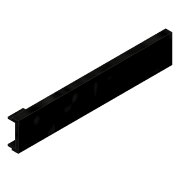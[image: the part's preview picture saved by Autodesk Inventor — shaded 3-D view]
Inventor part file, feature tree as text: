
AUTODESK INVENTOR PART (.ipt)
format: ipt  version: 2017 (Build 210142000, 142)  size: 198,144 bytes
history: native  units: in
note: dims shown in document units (in); Inventor stores cm internally (conversion verified against a paired STEP export)
features: sketch x6, extrude x6, projected_geometry x6, other x3, plane x2, reference x1
ambient origin geometry x8: Origin, YZ Plane, XZ Plane, XY Plane, X Axis, Y Axis, Z Axis, Center Point
bodies: Solid1 (feature_tree)
feature tree (24):
  sketch  "Sketch1"  dims[d0=0.02in d1=0.02in]
  plane  "Work Plane1"
  extrude  "Extrusion1"  Depth=0.02in
  plane  "Work Plane2"
  extrude  "Extrusion2"  Depth=0.025in
  extrude  "Extrusion3"  Depth=0.06in
  extrude  "Extrusion4"  Depth=0.02in
  extrude  "Extrusion5"  Depth=0.17in
  extrude  "Extrusion6"  Depth=0.05in
  reference  "Reference1"
  sketch  "Sketch2"  dims[d2=0.02in d3=0.025in]
  sketch  "Sketch3"  dims[d4=0.025in d5=0.06in]
  sketch  "Sketch4"  dims[d6=1.0in d7=0.0in d8=0.02in]
  sketch  "Sketch5"  dims[d9=0.17in d10=0.17in]
  projected_geometry  "Projected Loop1"
  sketch  "Sketch6"  dims[d11=0.02in d12=0.005in d13=0.005in d14=1.0in d15=0.0in d16=0.05in d17=1.0in d18=0.0in d19=0.02in d20=1.0in d21=0.0in d22=1.0in d23=0.0in d24=1.0in d25=0.0in]
  projected_geometry  "Projected Loop2"
  projected_geometry  "Projected Loop3"
  projected_geometry  "Projected Loop4"
  projected_geometry  "Projected Loop5"
  projected_geometry  "Projected Loop6"
  parser-record x1  (decoder bookkeeping rows leaked as tree rows — omitted from the tree; the rows remain in map.json)
  other  "Assembly1.iam"
  other  "Holder:1"
note: 1 file-system path scrubbed to <path> (originals preserved in map.json)
